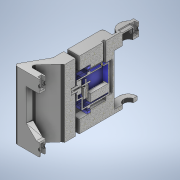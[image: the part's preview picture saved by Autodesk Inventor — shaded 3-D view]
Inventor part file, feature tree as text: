
AUTODESK INVENTOR PART (.ipt)
format: ipt  version: 2021 (Build 250183000, 183)  size: 3,784,192 bytes
history: mixed  units: in
note: dims shown in document units (in); Inventor stores cm internally (conversion verified against a paired STEP export)
features: extrude x6, sketch x6, move_body x5, other x4, plane x2, split x1, boolean_combine x1, imported_body x1
ambient origin geometry x8: Origin, YZ Plane, XZ Plane, XY Plane, X Axis, Y Axis, Z Axis, Center Point
bodies: Solid1 (imported_parasolid), Solid4 (imported_parasolid), Solid5 (imported_parasolid), Solid2 (imported_parasolid), Solid3 (imported_parasolid)
feature tree (26):
  other  "PenSlider"
  other  "MeshFeature1"
  plane  "Work Plane1"
  split  "Split2"
  move_body  "Move Body1"
  extrude  "Extrusion1"  TaperAngle=0.0deg  [1 undecoded]
  extrude  "Extrusion2"  Depth=0.4941in
  extrude  "Extrusion3"  Depth=0.5925in
  extrude  "Extrusion4"  Depth=1.2992in
  plane  "Work Plane2"
  extrude  "Extrusion5"  Depth=0.1969in TaperAngle=0.0deg
  extrude  "Extrusion6"  Depth=0.3937in
  other  "Servo-Rotation"
  other  "Servo-Static"
  boolean_combine  "Combine1"
  move_body  "Move Body2"
  move_body  "Move Body3"
  move_body  "Move Body4"
  move_body  "Move Body5"
  sketch  "Sketch1"  dims[d0=-0.0689in d1=0.0in d2=0.0in d3=-1.378in]
  sketch  "Sketch2"  dims[d4=0.9016in d5=0.4941in]
  sketch  "Sketch3"  dims[d6=0.1459in d9=0.5925in]
  sketch  "Sketch4"  dims[d10=0.6693in d11=0.0in d12=1.2992in]
  sketch  "Sketch5"  dims[d13=0.3445in d14=0.0in d15=0.1969in d16=0.0in]
  sketch  "Sketch6"  dims[d17=1.2677in d18=0.4843in d19=1.0827in d20=0.3346in d21=0.1907in d22=0.1272in d23=0.0in d24=0.2362in d25=0.0787in d26=0.1673in d27=0.0in d28=0.0in d29=0.0984in d30=0.1969in d31=0.1272in d32=0.0in d33=90.0deg d34=0.7764in d35=-0.2736in d36=1.6922in d37=0.0in d38=0.0in d39=0.3937in d40=0.0in d41=0.0in d42=-0.315in]
  imported_body  NMx_Import_Brep_tag  [imported B-rep: ~1903 faces, bbox_mm=[40.0, 53.000002, 78.240726]]
note: 1 required parameter value undecoded (feature->parameter linkage not recoverable at this tier; creation-order binding heuristic only, values carry confidence <= 0.55)
